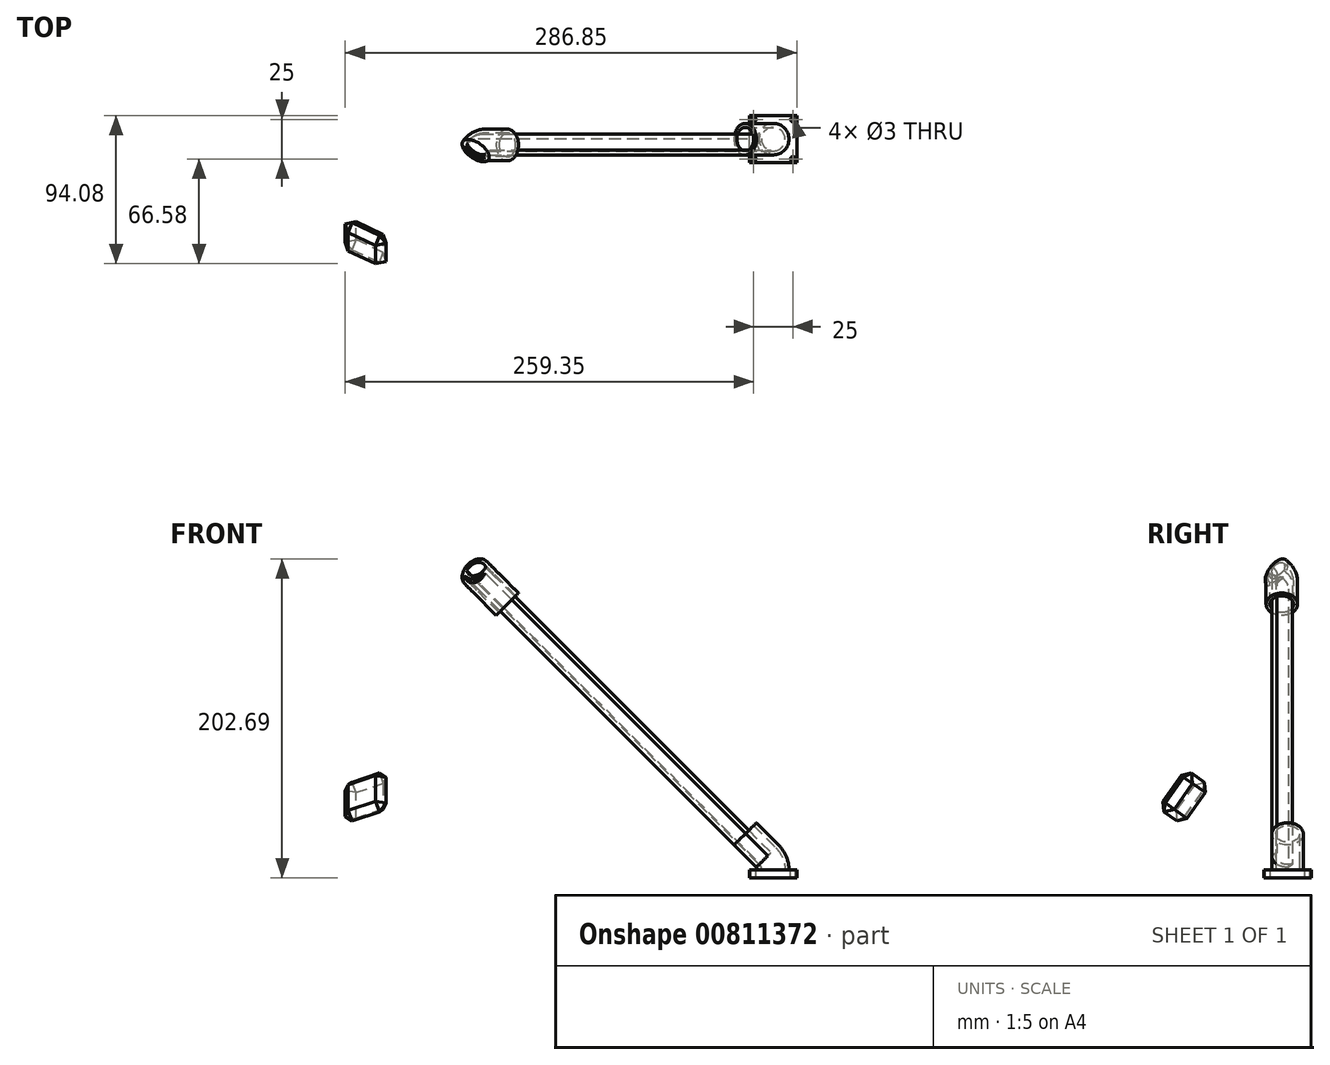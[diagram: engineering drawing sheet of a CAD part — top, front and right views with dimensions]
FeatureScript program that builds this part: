
annotation { "Feature Type Name" : "Feature", "Feature Type Description" : "" }
export const myFeature = defineFeature(function(context is Context, id is Id, definition is map)
    precondition{}
    {
        {
            var Q0;
            Q0=qCreatedBy(makeId("Top.planeOp"),FACE);
            var sketch = newSketch(context, id + "F0", { "sketchPlane" : qUnion([Q0])});
            skLineSegment(sketch, "E0.bottom", {"start": v(15, -15) * mm, "end": v(-15, -15) * mm});
            skLineSegment(sketch, "E0.top", {"start": v(15, 15) * mm, "end": v(-15, 15) * mm});
            skLineSegment(sketch, "E0.left", {"start": v(15, -15) * mm, "end": v(15, 15) * mm});
            skLineSegment(sketch, "E0.right", {"start": v(-15, -15) * mm, "end": v(-15, 15) * mm});
            skPoint(sketch, "E0.middle", {"position": v(0, 0) * mm});
            skLineSegment(sketch, "E1.bottom", {"start": v(12.5, -12.5) * mm, "end": v(-12.5, -12.5) * mm});
            skLineSegment(sketch, "E1.top", {"start": v(12.5, 12.5) * mm, "end": v(-12.5, 12.5) * mm});
            skLineSegment(sketch, "E1.left", {"start": v(12.5, -12.5) * mm, "end": v(12.5, 12.5) * mm});
            skLineSegment(sketch, "E1.right", {"start": v(-12.5, -12.5) * mm, "end": v(-12.5, 12.5) * mm});
            skCircle(sketch, "E2", {"center": v(-12.5, 12.5) * mm, "radius": 1.5 * mm});
            skCircle(sketch, "E3", {"center": v(12.5, 12.5) * mm, "radius": 1.5 * mm});
            skCircle(sketch, "E4", {"center": v(12.5, -12.5) * mm, "radius": 1.5 * mm});
            skCircle(sketch, "E5", {"center": v(-12.5, -12.5) * mm, "radius": 1.5 * mm});
            skCircle(sketch, "E6", {"center": v(0, 0) * mm, "radius": 7.5 * mm});
            skCircle(sketch, "E7", {"center": v(0, 0) * mm, "radius": 10 * mm});
            skSolve(sketch);
        }
        {
            var Q0;
            Q0=makeQuery(id+"F0.imprint","IMPRINT",FACE,{"disambiguationData":[TD([[makeQuery(id+"F0.imprint","IMPRINT",EDGE,{"derivedFrom":sQuery(id+"F0.wireOp",EDGE,"E0.bottom")}),-1.0]])]});
            var Q1;
            Q1=makeQuery(id+"F0.imprint","IMPRINT",FACE,{"disambiguationData":[TD([[makeQuery(id+"F0.imprint","IMPRINT",EDGE,{"derivedFrom":sQuery(id+"F0.wireOp",EDGE,"E7")}),-1.0]])]});
            var Q2;
            Q2=makeQuery(id+"F0.imprint","IMPRINT",FACE,{"disambiguationData":[TD([[makeQuery(id+"F0.imprint","IMPRINT",EDGE,{"derivedFrom":sQuery(id+"F0.wireOp",EDGE,"E6")}),-1.0]])]});
            var Q3;
            Q3=makeQuery(id+"F0.imprint","IMPRINT",FACE,{"disambiguationData":[TD([[makeQuery(id+"F0.imprint","IMPRINT",EDGE,{"derivedFrom":sQuery(id+"F0.wireOp",EDGE,"E6")}),1.0]])]});
            extrude(context, id + "F1", {"entities" : qUnion([Q0, Q1, Q2, Q3]), "oppositeDirection" : true, "depth" : 5 * mm, "offsetDistance" : 25 * mm});
        }
        {
            var Q0;
            Q0=makeQuery(id+"F0.imprint","IMPRINT",FACE,{"disambiguationData":[TD([[makeQuery(id+"F0.imprint","IMPRINT",EDGE,{"derivedFrom":sQuery(id+"F0.wireOp",EDGE,"E6")}),-1.0]])]});
            var Q1;
            Q1=sQuery(id+"F0.wireOp",EDGE,"E1.right");
            revolve(context, id + "F2", {"operationType" : NewBodyOperationType.ADD, "surfaceOperationType" : NewSurfaceOperationType.NEW, "entities" : qUnion([Q0]), "axis" : qUnion([Q1]), "revolveType" : RevolveType.ONE_DIRECTION, "oppositeDirection" : true, "angle" : 45 * degree});
        }
        {
            var Q0;
            Q0=makeQuery(id+"F2.opRevolve","CAP_FACE",FACE,{"disambiguationData":[OSD([sQuery(id+"F0.wireOp",EDGE,"E6"),sQuery(id+"F0.wireOp",EDGE,"E7")])],"isStart":false});
            var sketch = newSketch(context, id + "F3", { "sketchPlane" : qUnion([Q0])});
            skCircle(sketch, "E8.0.0", {"center": v(3.66, 0) * mm, "radius": 10 * mm});
            skCircle(sketch, "E9.0", {"center": v(3.66, 0) * mm, "radius": 7.5 * mm});
            skSolve(sketch);
        }
        {
            var Q0;
            Q0=makeQuery(id+"F2.opRevolve","CAP_FACE",FACE,{"disambiguationData":[OSD([sQuery(id+"F0.wireOp",EDGE,"E6"),sQuery(id+"F0.wireOp",EDGE,"E7")])],"isStart":false});
            extrude(context, id + "F4", {"entities" : qUnion([Q0]), "operationType" : NewBodyOperationType.ADD, "depth" : 20 * mm, "offsetDistance" : 25 * mm});
        }
        {
            var Q0;
            Q0=makeQuery(id+"F3.imprint","IMPRINT",FACE,{"disambiguationData":[TD([[makeQuery(id+"F3.imprint","IMPRINT",EDGE,{"derivedFrom":sQuery(id+"F3.wireOp",EDGE,"E9.0")}),1.0]])]});
            extrude(context, id + "F5", {"entities" : qUnion([Q0]), "depth" : 250 * mm, "offsetDistance" : 25 * mm});
        }
        {
            var Q0;
            Q0=makeQuery(id+"F5.opExtrude","CAP_FACE",FACE,{"disambiguationData":[OSD([sQuery(id+"F3.wireOp",EDGE,"E9.0")])],"isStart":false});
            var sketch = newSketch(context, id + "F6", { "sketchPlane" : qUnion([Q0])});
            skCircle(sketch, "E10.0", {"center": v(3.66, 0) * mm, "radius": 7.5 * mm});
            skCircle(sketch, "E11", {"center": v(3.66, 0) * mm, "radius": 10 * mm});
            skLineSegment(sketch, "E12", {"start": v(15.66, 13.72) * mm, "end": v(15.66, -14.26) * mm});
            skSolve(sketch);
        }
        {
            var Q0;
            Q0=makeQuery(id+"F6.imprint","IMPRINT",FACE,{"disambiguationData":[TD([[makeQuery(id+"F6.imprint","IMPRINT",EDGE,{"derivedFrom":sQuery(id+"F6.wireOp",EDGE,"E10.0")}),-1.0]])]});
            var Q1;
            Q1=makeQuery(id+"F6.imprint","IMPRINT",FACE,{"disambiguationData":[TD([[makeQuery(id+"F6.imprint","IMPRINT",EDGE,{"derivedFrom":sQuery(id+"F6.wireOp",EDGE,"E10.0")}),1.0]])]});
            var Q2;
            Q2=sQuery(id+"F6.wireOp",EDGE,"E12");
            revolve(context, id + "F7", {"surfaceOperationType" : NewSurfaceOperationType.NEW, "entities" : qUnion([Q0, Q1]), "axis" : qUnion([Q2]), "revolveType" : RevolveType.ONE_DIRECTION, "oppositeDirection" : true, "angle" : 45 * degree});
        }
        {
            var Q0;
            Q0=makeQuery(id+"F6.imprint","IMPRINT",FACE,{"disambiguationData":[TD([[makeQuery(id+"F6.imprint","IMPRINT",EDGE,{"derivedFrom":sQuery(id+"F6.wireOp",EDGE,"E10.0")}),-1.0]])]});
            extrude(context, id + "F8", {"entities" : qUnion([Q0]), "operationType" : NewBodyOperationType.ADD, "oppositeDirection" : true, "depth" : 20 * mm, "offsetDistance" : 25 * mm});
        }
        {
            var Q0;
            Q0=makeQuery(id+"F7.opRevolve","CAP_FACE",FACE,{"disambiguationData":[OSD([sQuery(id+"F6.wireOp",EDGE,"E11")])],"isStart":false});
            var sketch = newSketch(context, id + "F9", { "sketchPlane" : qUnion([Q0])});
            skCircle(sketch, "E13.0", {"center": v(-183.95, 0) * mm, "radius": 10 * mm});
            skLineSegment(sketch, "E14.bottom", {"start": v(-168.95, -15) * mm, "end": v(-198.95, -15) * mm});
            skLineSegment(sketch, "E14.top", {"start": v(-168.95, 15) * mm, "end": v(-198.95, 15) * mm});
            skLineSegment(sketch, "E14.left", {"start": v(-168.95, -15) * mm, "end": v(-168.95, 15) * mm});
            skLineSegment(sketch, "E14.right", {"start": v(-198.95, -15) * mm, "end": v(-198.95, 15) * mm});
            skSolve(sketch);
        }
        {
            var Q0;
            Q0=makeQuery(id+"F9.imprint","IMPRINT",FACE,{"disambiguationData":[TD([[makeQuery(id+"F9.imprint","IMPRINT",EDGE,{"derivedFrom":sQuery(id+"F9.wireOp",EDGE,"E13.0")}),1.0]])]});
            var Q1;
            Q1=makeQuery(id+"F9.imprint","IMPRINT",FACE,{"disambiguationData":[TD([[makeQuery(id+"F9.imprint","IMPRINT",EDGE,{"derivedFrom":sQuery(id+"F9.wireOp",EDGE,"E13.0")}),-1.0]])]});
            extrude(context, id + "F10", {"entities" : qUnion([Q0, Q1]), "operationType" : NewBodyOperationType.ADD, "depth" : 10 * mm, "offsetDistance" : 25 * mm});
        }
        {
            var Q0;
            Q0=makeQuery(id+"F10.opExtrude","SWEPT_FACE",FACE,{"disambiguationData":[OSD([sQuery(id+"F9.wireOp",EDGE,"E14.right")])]});
            var Q1;
            Q1=makeQuery(id+"F10.opExtrude","SWEPT_FACE",FACE,{"disambiguationData":[OSD([sQuery(id+"F9.wireOp",EDGE,"E14.top")])]});
            var Q2;
            Q2=makeQuery(id+"F10.opExtrude","SWEPT_FACE",FACE,{"disambiguationData":[OSD([sQuery(id+"F9.wireOp",EDGE,"E14.left")])]});
            var Q3;
            Q3=makeQuery(id+"F10.opExtrude","SWEPT_FACE",FACE,{"disambiguationData":[OSD([sQuery(id+"F9.wireOp",EDGE,"E14.bottom")])]});
            chamfer(context, id + "F11", {"entities" : qUnion([Q0, Q1, Q2, Q3]), "width" : 5 * mm, "tangentPropagation" : true});
        }
    });
